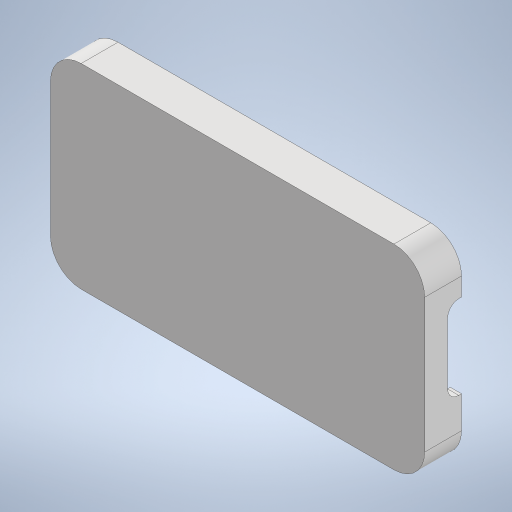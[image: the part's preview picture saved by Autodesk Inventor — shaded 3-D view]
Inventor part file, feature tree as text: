
AUTODESK INVENTOR PART (.ipt)
format: ipt  version: 2023 (Build 270158000, 158)  size: 316,928 bytes
history: native  units: in
note: dims shown in document units (in); Inventor stores cm internally (conversion verified against a paired STEP export)
features: reference x13, extrude x5, sketch x5, fillet x4, other x4, projected_geometry x2, plane x1
ambient origin geometry x8: Origin, YZ Plane, XZ Plane, XY Plane, X Axis, Y Axis, Z Axis, Center Point
bodies: Solid1 (feature_tree)
feature tree (34):
  extrude  "Extrusion1"  Depth=0.1102in
  extrude  "Extrusion2"  Depth=0.1181in
  fillet  "Fillet1"  Radius=0.1181in
  sketch  "Sketch3"  dims[d6=0.0787in d7=0.0in d8=0.1181in]
  plane  "Work Plane1"
  extrude  "Extrusion3"  Depth=0.1181in
  extrude  "Extrusion4"  Depth=0.2963in TaperAngle=0.0deg
  extrude  "Extrusion5"  Depth=0.3937in TaperAngle=0.0deg
  fillet  "Fillet2"  Radius=0.0984in
  fillet  "Fillet3"  Radius=0.8563in
  fillet  "Fillet4"  Radius=0.0787in
  sketch  "Sketch1"  dims[d0=0.2362in d1=0.1102in]
  reference  "Reference1"
  reference  "Reference2"
  reference  "Reference3"
  reference  "Reference4"
  reference  "Reference5"
  reference  "Reference6"
  reference  "Reference7"
  sketch  "Sketch2"  dims[d2=0.1102in d3=0.1102in d4=0.1181in d5=0.0in]
  reference  "Reference8"
  reference  "Reference9"
  reference  "Reference10"
  reference  "Reference11"
  projected_geometry  "Projected Loop1"
  sketch  "Sketch4"  dims[d9=0.0984in d10=0.2963in d11=0.0in]
  projected_geometry  "Projected Loop2"
  sketch  "Sketch5"  dims[d12=0.0197in d13=0.3937in d14=0.0in d15=0.0984in d16=0.8563in d17=0.0in d18=0.0787in d19=0.0787in d20=0.0787in]
  reference  "Reference12"
  reference  "Reference13"
  other  "<userpath>\Nextcloud2\private\HAMpower\Case\case_assambly.iam"
  other  "case_assambly.iam"
  other  "powerplay:1"
  other  "Case_Cap:1"
